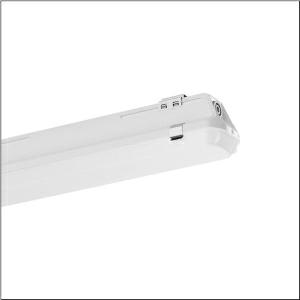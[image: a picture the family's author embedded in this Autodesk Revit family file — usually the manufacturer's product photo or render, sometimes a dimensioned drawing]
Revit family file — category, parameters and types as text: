
# Revit family: monsun_r__11_51fp208p460h_1e38
name_source: partatom
category: Lighting Fixtures
units: mm (PartAtom-declared; Revit-internal decimal feet)

## family parameters
Cut with Voids When Loaded = No
Host = Face
Light Source = No
Part Type = Normal
Room Calculation Point = No
Round Connector Dimension = Use Diameter
Shared = No

## types (1)
- Monsun® 11 (1 x LED, 5490 lm, 33.9 W, 4000K)
    Apparent Load = 34 VA
    CIE Flux Codes = 45 75 93 94 100
    Color Rendering = 80
    Color Temperature = 4000K
    Default Elevation = 1800 mm
    Description = Monsun® 11, damp-proof luminaire, chain hanger, primary optical cover: enclosure, of PC, light emission: direct distribution, primary light characteristic: symmetric, installation type: suspended mounting, surface-mounted, horizontal mounting, vertical mounting, LED, rated luminous flux: 5.490lm, luminous efficacy: 162lm/W, light colour: 840, colour temperature: 4000K, control gear: ECG, with terminal, 3-pole, max. 2.5mm², mains connection: 220..240V, AC, 50/60Hz, rated input power: 34W, luminaire housing, of glass-fibre reinforced polyester, uncoated, bright grey, incl. chain hanger, length: 1.590mm, width: 90mm, height: 88mm, clip for enclosure, of stainless steel (V2A), ceiling mounting element, of stainless steel (V2A), chain hanger, of stainless steel (V2A), protection rating (complete): IP66, insulation class (complete): insulation class I (protective earthing), certification: CE, ENEC, VDE, UKCA, protection symbol: D, impact resistance: IK08, permissible operating ambient temperature: -35..+40°C, standard: EN 50419, EN 60598-2-1, no direct snow, no direct sun, no direct rain, for indoor or canopied outdoor use, corresponds to IFS (International Featured Standards) requirements for safety and quality in the food industry, contact your sales advisor before using the luminaires in applications with unclear chemical exposure, large temperature fluctuations or condensation-forming humidity, LABS conformity tested according to VDMA 24364:2018-05, packaging unit: 1 piece
    Height = 89 mm
    Lamp = 1 x LED
    Lamp Light Flux = 5490 lm
    Lamp Power = 33.9 W
    Lamp count = 1
    Length = 1590 mm
    Luminous efficacy = 162 lm/W
    Manufacturer = Siteco
    ModVariant = No
    Model = 51FP208P460H
    Mounting Place = Ceiling
    Mounting Type = Surface mounted
    Number of Poles = 1
    OnlyDefault = Yes
    Power Factor = 1
    Product Name = Monsun® 11
    Product group = damp-proof luminaire
    ProductGroupID = 300
    Protection Class = Protection class I
    Protection Degree = IP 66
    RLX_Detail_Level = 1
    RLX_Emergency_Light_Flux = 0 lm
    RLX_Emergency_Type = 0
    RLX_Emergency_Type_DB = No
    RlxData = <blob elided: 88677 chars, md5=8489eb21>
    Socket = socket
    Standby Power = 0 W
    System Light Flux = 5490 lm
    System Power = 34 W
    Type Comments = Product without accessories
    Type Image = l_1319650.jpg
    URL = http://relux.com
    VarID = ---
    Voltage = 0 V
    Weight = 0.00 kg
    Width = 90 mm

## geometry (parser evidence)
native form markers: Blend x4, Sweep x14
no freeform markers — native parametric forms only
